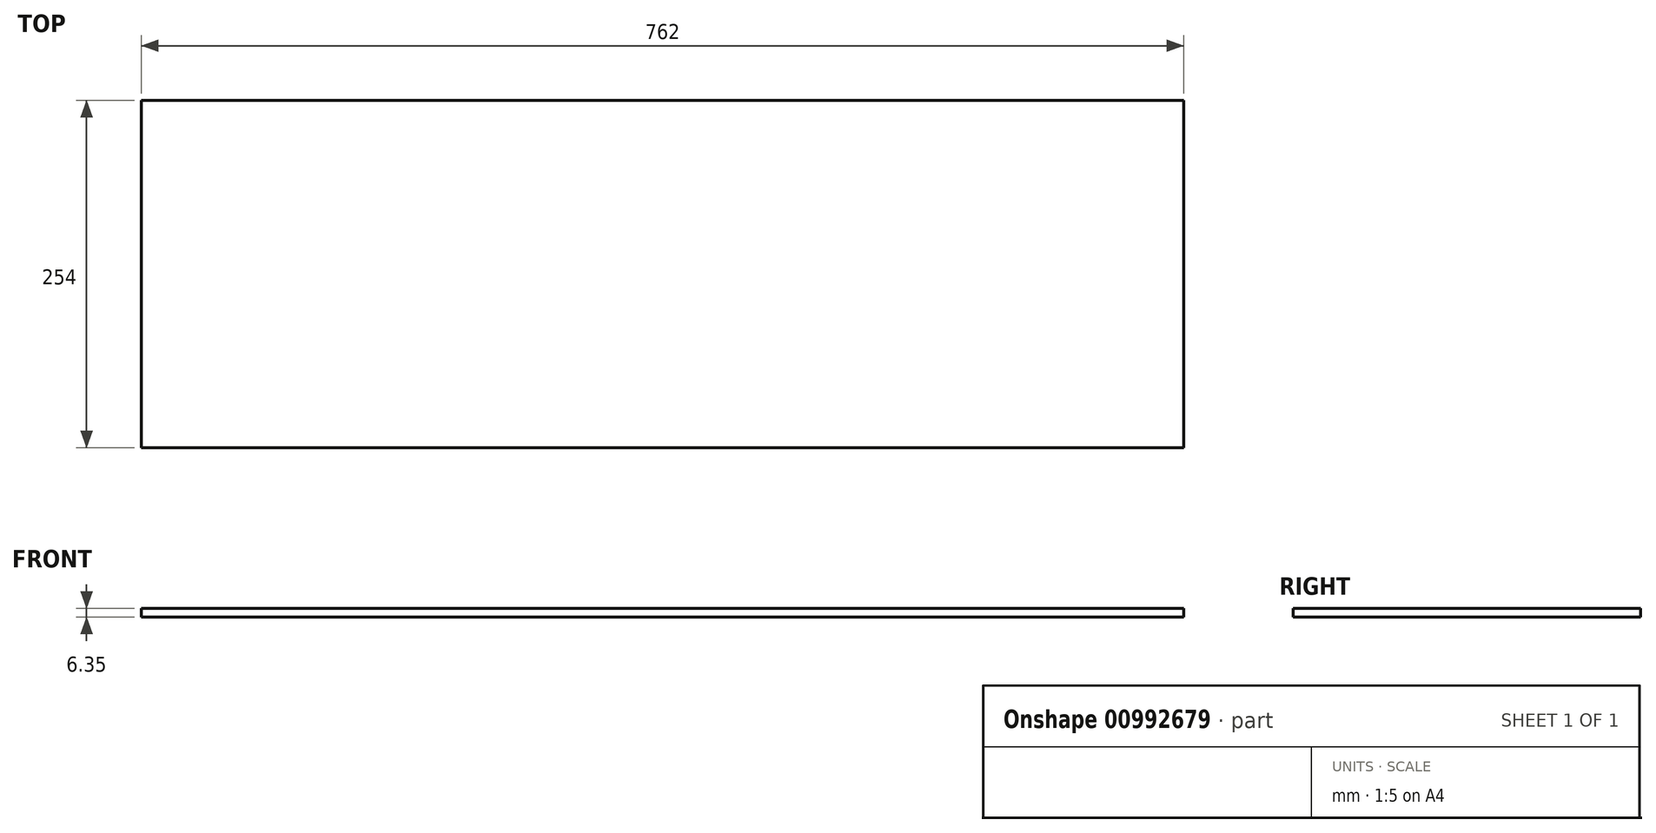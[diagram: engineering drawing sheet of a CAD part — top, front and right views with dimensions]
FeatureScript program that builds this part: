
annotation { "Feature Type Name" : "Feature", "Feature Type Description" : "" }
export const myFeature = defineFeature(function(context is Context, id is Id, definition is map)
    precondition{}
    {
        {
            var Q0;
            Q0=qCreatedBy(makeId("Top.planeOp"),FACE);
            var sketch = newSketch(context, id + "F0", { "sketchPlane" : qUnion([Q0])});
            skLineSegment(sketch, "E0.bottom", {"start": v(-738.81, 225.96) * mm, "end": v(23.19, 225.96) * mm});
            skLineSegment(sketch, "E0.top", {"start": v(-738.81, -28.04) * mm, "end": v(23.19, -28.04) * mm});
            skLineSegment(sketch, "E0.left", {"start": v(-738.81, 225.96) * mm, "end": v(-738.81, -28.04) * mm});
            skLineSegment(sketch, "E0.right", {"start": v(23.19, 225.96) * mm, "end": v(23.19, -28.04) * mm});
            skSolve(sketch);
        }
        {
            var Q0;
            Q0=makeQuery(id+"F0.imprint","IMPRINT",FACE,{"disambiguationData":[TD([[makeQuery(id+"F0.imprint","IMPRINT",EDGE,{"derivedFrom":sQuery(id+"F0.wireOp",EDGE,"E0.bottom")}),-1.0]])]});
            extrude(context, id + "F1", {"entities" : qUnion([Q0]), "depth" : 6.35 * mm, "offsetDistance" : 25.4 * mm});
        }
    });
